# Revit family: Gleiter GL-100, 1xM10-M12, V4A
name_source: partatom
category: HLS-Bauteile
units: mm (PartAtom-declared; Revit-internal decimal feet)

## family parameters
Arbeitsebenenbasiert = Ja
Beim Laden mit Abzugskörper schneiden = Nein
Bemaßung runder Anschluss = Durchmesser verwenden
Beschriftungsausrichtung beibehalten = Nein
Gemeinsam genutzt = Ja
Immer vertikal = Nein
Raumberechnungspunkt = Nein
Teiletyp = Normal

## types (2) — shared parameters
Anzahl Anschlüsse = 1
B = 160 mm  [stored 0.524934 ft]
B1 = 58 mm  [stored 0.190289 ft]
Breite = 66 mm  [stored 0.216535 ft]
Fabrikat = MEFA
Firma = MEFA Befestigungs- und Montagesysteme GmbH
Gleitreibungsfaktor = 0,15 - 0,25
H1 = 15 mm  [stored 0.0492126 ft]
Haftreibungsfaktor = 0,2 - 0,3
Kurztext1 = Gleiter axial GL 100 V4A
L1 = 80 mm  [stored 0.262467 ft]
L2 = 120 mm
Lochdurchmesser = 13 mm
Länge = 160 mm  [stored 0.524934 ft]
MD = 3 mm  [stored 0.00984252 ft]
Material Gleitelement = Edelstahl
Material Gleitstreifen = Kunststoff
Materialname Gleitelement = V4A
Materialname Gleitstreifen = Polyamid 6
Mengeneinheit = St
Vorgabe-Ansicht = 1219 mm
max. Schiebeweg axial = 68 mm
max. Temperaturbeständigkeit = 100 °C
vpe = 1

## per-type parameters (varying)
| type | AG | Anschluss | Artikelnummer | EAN | Gewicht | Gewicht pro Bauteil | Gewinde | Kurztext2 |
| Gleiter GL 100, 1x M10, V4A | 6kt-Mutter parametrik : A2 Mutter M10 (4128110) | 1 x M10 | 0770550 | 4250928463593 | 0.43 kg | 0.43 kg | M10 | Anschluss 1 x M10 |
| Gleiter GL 100, 1x M12, V4A | 6kt-Mutter parametrik : A2 Mutter M12 (4128112) | 1 x M12 | 0770552 | 4250928463609 | 0.44 kg | 0.44 kg | M12 | Anschluss 1 x M12 |

note: [stored X ft] marks values corroborated as IEEE doubles in the binary element streams (Revit-internal decimal feet)

## geometry (parser evidence)
native form markers: Sweep x2
no freeform markers — native parametric forms only
